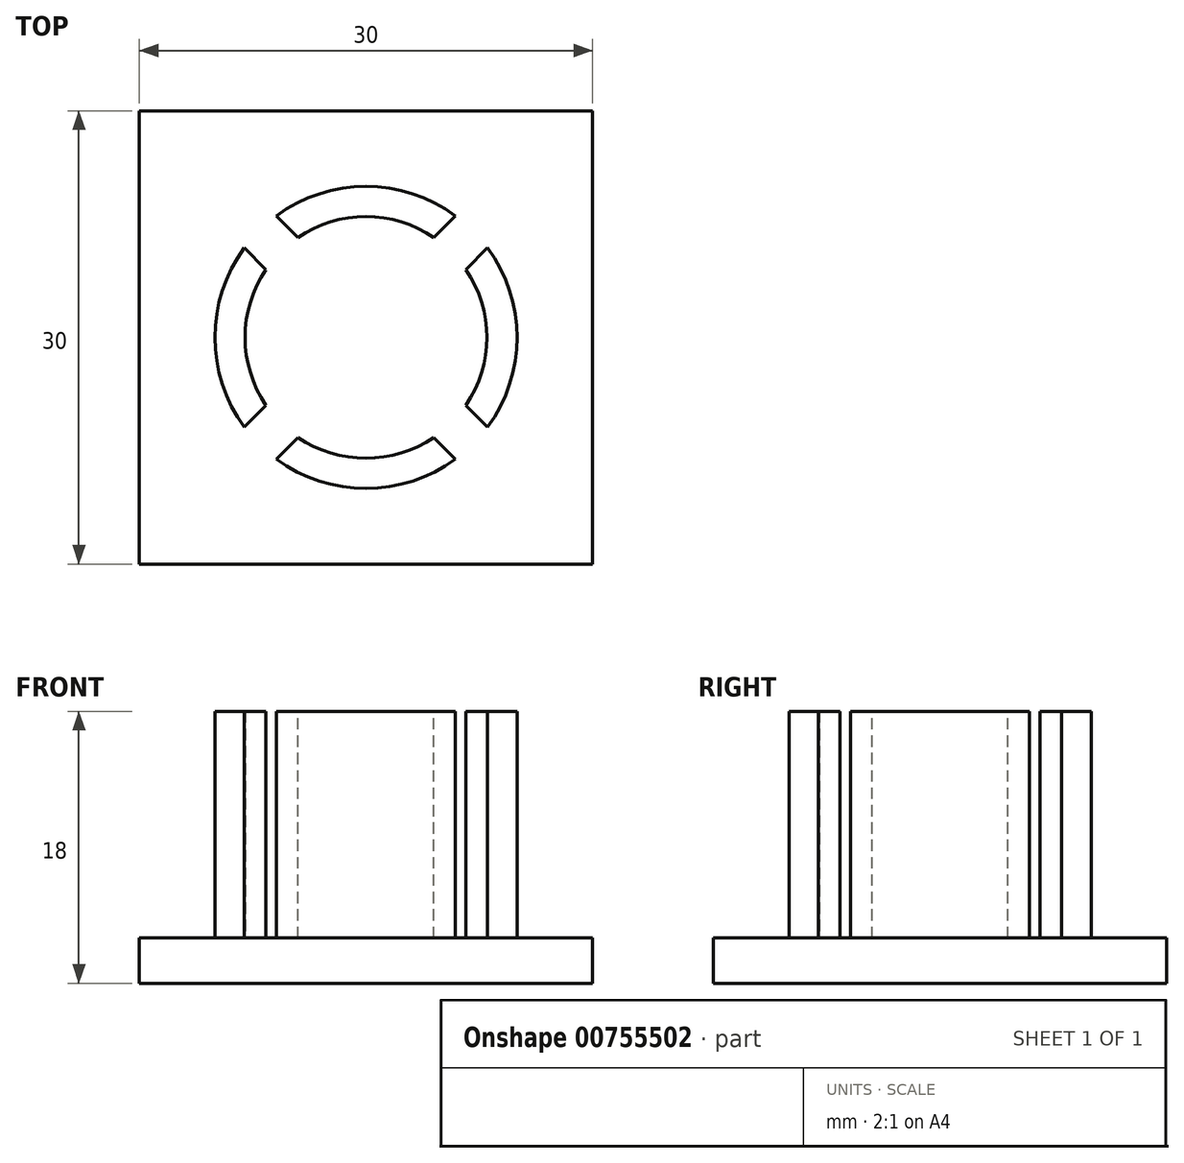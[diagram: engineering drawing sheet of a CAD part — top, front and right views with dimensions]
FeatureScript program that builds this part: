
annotation { "Feature Type Name" : "Feature", "Feature Type Description" : "" }
export const myFeature = defineFeature(function(context is Context, id is Id, definition is map)
    precondition{}
    {
        {
            var Q0;
            Q0=qCreatedBy(makeId("Top.planeOp"),FACE);
            var sketch = newSketch(context, id + "F0", { "sketchPlane" : qUnion([Q0])});
            skLineSegment(sketch, "E0.bottom", {"start": v(15, -15) * mm, "end": v(-15, -15) * mm});
            skLineSegment(sketch, "E0.top", {"start": v(15, 15) * mm, "end": v(-15, 15) * mm});
            skLineSegment(sketch, "E0.left", {"start": v(15, -15) * mm, "end": v(15, 15) * mm});
            skLineSegment(sketch, "E0.right", {"start": v(-15, -15) * mm, "end": v(-15, 15) * mm});
            skPoint(sketch, "E0.middle", {"position": v(0, 0) * mm});
            skSolve(sketch);
        }
        {
            var Q0;
            Q0=makeQuery(id+"F0.imprint","IMPRINT",FACE,{"disambiguationData":[TD([[makeQuery(id+"F0.imprint","IMPRINT",EDGE,{"derivedFrom":sQuery(id+"F0.wireOp",EDGE,"E0.bottom")}),-1.0]])]});
            extrude(context, id + "F1", {"entities" : qUnion([Q0]), "depth" : 3 * mm, "offsetDistance" : 25 * mm});
        }
        {
            var Q0;
            Q0=makeQuery(id+"F1.opExtrude","CAP_FACE",FACE,{"disambiguationData":[OSD([sQuery(id+"F0.wireOp",EDGE,"E0.bottom"),sQuery(id+"F0.wireOp",EDGE,"E0.top"),sQuery(id+"F0.wireOp",EDGE,"E0.left"),sQuery(id+"F0.wireOp",EDGE,"E0.right")])],"isStart":false});
            var sketch = newSketch(context, id + "F2", { "sketchPlane" : qUnion([Q0])});
            skCircle(sketch, "E1", {"center": v(0, 0) * mm, "radius": 10 * mm});
            skCircle(sketch, "E2", {"center": v(0, 0) * mm, "radius": 8 * mm});
            skSolve(sketch);
        }
        {
            var Q0;
            Q0 = qSketchRegion(id + "F2", true);
            extrude(context, id + "F3", {"entities" : qUnion([Q0]), "operationType" : NewBodyOperationType.ADD, "depth" : 15 * mm, "offsetDistance" : 25 * mm});
        }
        {
            var Q0;
            Q0=makeQuery(id+"F3.opExtrude","CAP_FACE",FACE,{"disambiguationData":[OSD([sQuery(id+"F2.wireOp",EDGE,"E1"),sQuery(id+"F2.wireOp",EDGE,"E2")])],"isStart":false});
            var sketch = newSketch(context, id + "F4", { "sketchPlane" : qUnion([Q0])});
            skLineSegment(sketch, "E3", {"start": v(0, 14.23) * mm, "end": v(0, -14.63) * mm, "construction": true});
            skLineSegment(sketch, "E4", {"start": v(-17.3, 0) * mm, "end": v(18.52, 0) * mm, "construction": true});
            skLineSegment(sketch, "E5", {"start": v(0, 0) * mm, "end": v(-10.46, 10.46) * mm, "construction": true});
            skLineSegment(sketch, "E6", {"start": v(-5.93, 8.05) * mm, "end": v(-4.5, 6.62) * mm});
            skLineSegment(sketch, "E7", {"start": v(-8.05, 5.93) * mm, "end": v(-6.62, 4.5) * mm});
            skLineSegment(sketch, "E8.1.0", {"start": v(-5.93, -8.05) * mm, "end": v(-4.5, -6.62) * mm});
            skLineSegment(sketch, "E8.1.1", {"start": v(-8.05, -5.93) * mm, "end": v(-6.62, -4.5) * mm});
            skLineSegment(sketch, "E8.2.0", {"start": v(8.05, -5.93) * mm, "end": v(6.62, -4.5) * mm});
            skLineSegment(sketch, "E8.2.1", {"start": v(5.93, -8.05) * mm, "end": v(4.5, -6.62) * mm});
            skPoint(sketch, "E8.center", {"position": v(0, 0) * mm});
            skLineSegment(sketch, "E9.2.3.0", {"start": v(5.93, 8.05) * mm, "end": v(4.5, 6.62) * mm});
            skLineSegment(sketch, "E9.3.3.0", {"start": v(8.05, 5.93) * mm, "end": v(6.62, 4.5) * mm});
            skSolve(sketch);
        }
        {
            var Q0;
            {var subQ0=sQuery(id+"F4.wireOp",EDGE,"E6");Q0=makeQuery(id+"F4.imprint","IMPRINT",FACE,{"disambiguationData":[TD([[makeQuery(id+"F4.imprint","IMPRINT",EDGE,{"derivedFrom":subQ0}),-1.0]])]});}
            var Q1;
            {var subQ0=sQuery(id+"F4.wireOp",EDGE,"E9.2.3.0");Q1=makeQuery(id+"F4.imprint","IMPRINT",FACE,{"disambiguationData":[TD([[makeQuery(id+"F4.imprint","IMPRINT",EDGE,{"derivedFrom":subQ0}),1.0]])]});}
            var Q2;
            {var subQ0=sQuery(id+"F4.wireOp",EDGE,"E8.2.0");Q2=makeQuery(id+"F4.imprint","IMPRINT",FACE,{"disambiguationData":[TD([[makeQuery(id+"F4.imprint","IMPRINT",EDGE,{"derivedFrom":subQ0}),1.0]])]});}
            var Q3;
            {var subQ0=sQuery(id+"F4.wireOp",EDGE,"E8.1.0");Q3=makeQuery(id+"F4.imprint","IMPRINT",FACE,{"disambiguationData":[TD([[makeQuery(id+"F4.imprint","IMPRINT",EDGE,{"derivedFrom":subQ0}),1.0]])]});}
            var Q4;
            {var subQ0=sQuery(id+"F0.wireOp",EDGE,"E0.left");var subQ1=sQuery(id+"F0.wireOp",EDGE,"E0.top");var subQ2=sQuery(id+"F0.wireOp",EDGE,"E0.right");var subQ3=sQuery(id+"F0.wireOp",EDGE,"E0.bottom");Q4=makeQuery(id+"F3.boolean.opBoolean","SPLIT",FACE,{"disambiguationData":[TD([makeQuery(id+"F1.opExtrude","SWEPT_FACE",FACE,{"disambiguationData":[OSD([subQ3])]})])],"derivedFrom":makeQuery(id+"F1.opExtrude","CAP_FACE",FACE,{"disambiguationData":[OSD([subQ3,subQ1,subQ0,subQ2])],"isStart":false})});}
            extrude(context, id + "F5", {"entities" : qUnion([Q0, Q1, Q2, Q3]), "operationType" : NewBodyOperationType.REMOVE, "endBound" : BoundingType.UP_TO_SURFACE, "oppositeDirection" : true, "depth" : 25 * mm, "endBoundEntityFace" : qUnion([Q4]), "offsetDistance" : 25 * mm});
        }
    });
